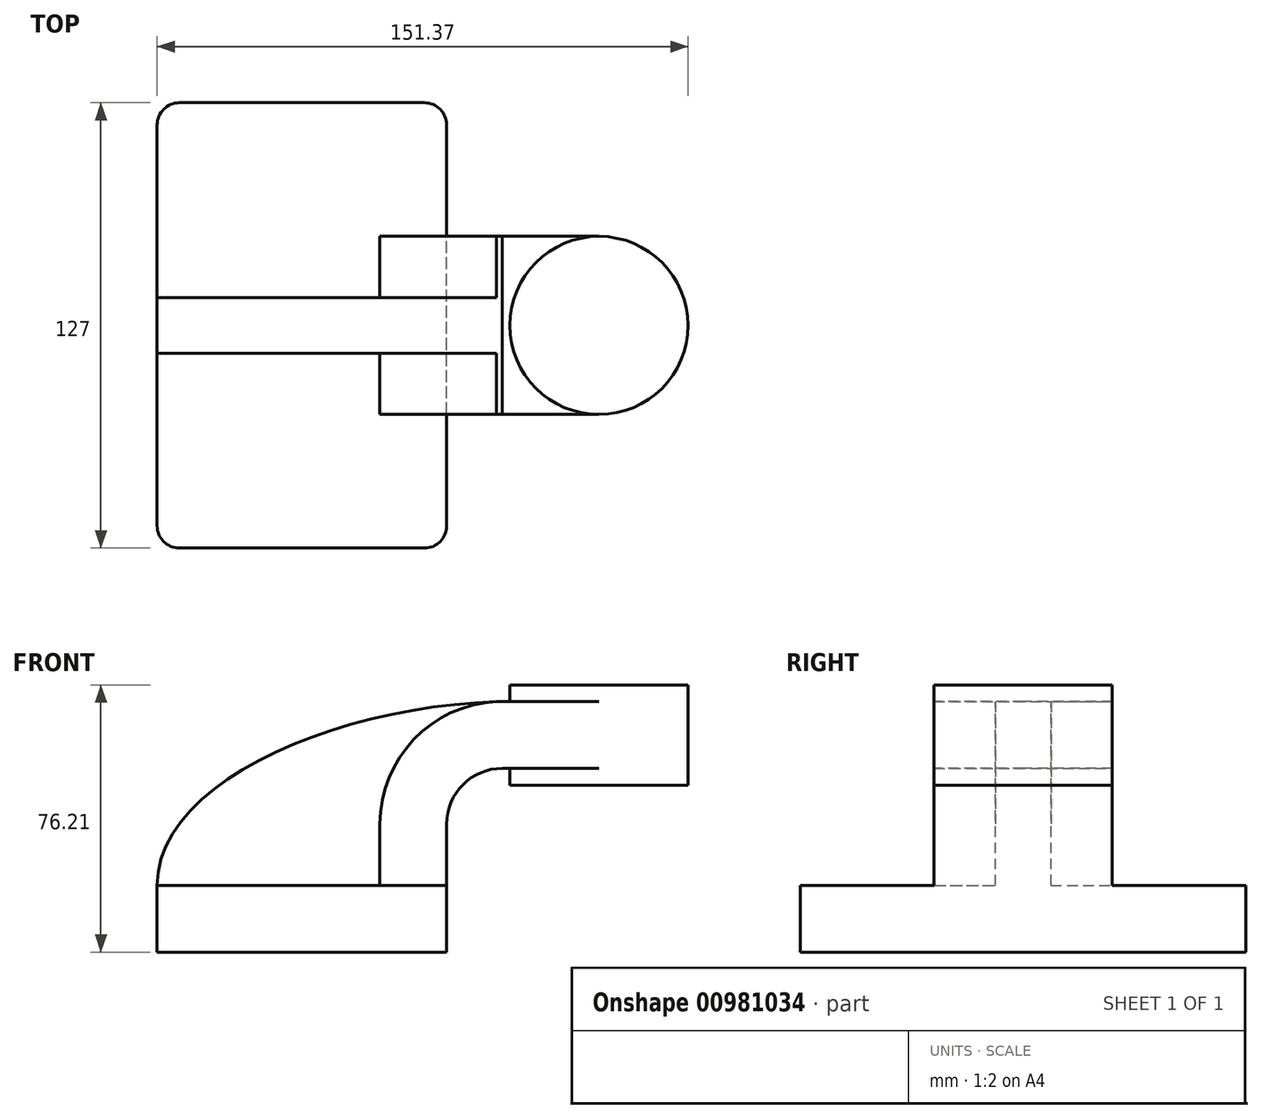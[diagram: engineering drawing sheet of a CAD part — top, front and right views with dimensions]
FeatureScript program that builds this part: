
annotation { "Feature Type Name" : "Feature", "Feature Type Description" : "" }
export const myFeature = defineFeature(function(context is Context, id is Id, definition is map)
    precondition{}
    {
        {
            var Q0;
            Q0=qCreatedBy(makeId("Front.planeOp"),FACE);
            var sketch = newSketch(context, id + "F0", { "sketchPlane" : qUnion([Q0])});
            skLineSegment(sketch, "E0.bottom", {"start": v(-41.28, 9.52) * mm, "end": v(41.28, 9.53) * mm});
            skLineSegment(sketch, "E0.top", {"start": v(-41.27, -9.52) * mm, "end": v(41.28, -9.52) * mm});
            skLineSegment(sketch, "E0.left", {"start": v(-41.28, 9.52) * mm, "end": v(-41.28, -9.52) * mm});
            skLineSegment(sketch, "E0.right", {"start": v(41.27, 9.53) * mm, "end": v(41.28, -9.52) * mm});
            skPoint(sketch, "E0.middle", {"position": v(0, 0) * mm});
            skLineSegment(sketch, "E1.bottom", {"start": v(110.09, 38.1) * mm, "end": v(59.29, 38.1) * mm});
            skLineSegment(sketch, "E1.top", {"start": v(110.09, 66.68) * mm, "end": v(59.29, 66.68) * mm});
            skLineSegment(sketch, "E1.left", {"start": v(110.09, 38.1) * mm, "end": v(110.09, 66.68) * mm});
            skLineSegment(sketch, "E1.right", {"start": v(59.29, 38.1) * mm, "end": v(59.29, 66.68) * mm});
            skPoint(sketch, "E1.middle", {"position": v(84.69, 52.39) * mm});
            skLineSegment(sketch, "E2", {"start": v(41.27, 9.53) * mm, "end": v(41.27, 27) * mm});
            skArc(sketch, "E3", {"start": v(41.27, 27) * mm, "mid": v(45.92, 38.23) * mm, "end": v(57.15, 42.88) * mm});
            skLineSegment(sketch, "E4", {"start": v(57.15, 42.88) * mm, "end": v(84.69, 42.88) * mm});
            skPoint(sketch, "E4.endSnap0", {"position": v(84.69, 38.1) * mm});
            skLineSegment(sketch, "E5.0", {"start": v(57.15, 61.93) * mm, "end": v(84.69, 61.93) * mm});
            skArc(sketch, "E5.1", {"start": v(22.22, 27) * mm, "mid": v(32.45, 51.7) * mm, "end": v(57.15, 61.93) * mm});
            skLineSegment(sketch, "E5.2", {"start": v(22.22, 9.53) * mm, "end": v(22.22, 27) * mm});
            skLineSegment(sketch, "E6", {"start": v(84.69, 38.1) * mm, "end": v(84.69, 66.68) * mm});
            skFitSpline(sketch, "E7", {"points": [v(-41.28, 9.53) * mm, v(57.15, 61.93) * mm], "startDerivative": vector(0.15, 89.7) * mm, "endDerivative": vector(137.76, 2.53) * mm});
            skSolve(sketch);
        }
        {
            var Q0;
            Q0=makeQuery(id+"F0.imprint","IMPRINT",FACE,{"disambiguationData":[TD([[makeQuery(id+"F0.imprint","IMPRINT",EDGE,{"derivedFrom":sQuery(id+"F0.wireOp",EDGE,"E0.top")}),1.0]])]});
            extrude(context, id + "F1", {"entities" : qUnion([Q0]), "endBound" : BoundingType.SYMMETRIC, "depth" : 127 * mm, "offsetDistance" : 25.4 * mm});
        }
        {
            var Q0;
            {var subQ3=sQuery(id+"F0.wireOp",EDGE,"E5.2");Q0=makeQuery(id+"F0.imprint","IMPRINT",FACE,{"disambiguationData":[TD([[makeQuery(id+"F0.imprint","IMPRINT",EDGE,{"derivedFrom":subQ3}),1.0]])]});}
            extrude(context, id + "F2", {"entities" : qUnion([Q0]), "operationType" : NewBodyOperationType.ADD, "endBound" : BoundingType.SYMMETRIC, "depth" : 15.88 * mm, "offsetDistance" : 25.4 * mm});
        }
        {
            var Q0;
            Q0=makeQuery(id+"F1.opExtrude","CAP_EDGE",EDGE,{"disambiguationData":[OSD([sQuery(id+"F0.wireOp",EDGE,"E0.left")])],"isStart":false});
            var Q1;
            Q1=makeQuery(id+"F1.opExtrude","CAP_EDGE",EDGE,{"disambiguationData":[OSD([sQuery(id+"F0.wireOp",EDGE,"E0.right")])],"isStart":false});
            var Q2;
            Q2=makeQuery(id+"F1.opExtrude","CAP_EDGE",EDGE,{"disambiguationData":[OSD([sQuery(id+"F0.wireOp",EDGE,"E0.right")])],"isStart":true});
            var Q3;
            Q3=makeQuery(id+"F1.opExtrude","CAP_EDGE",EDGE,{"disambiguationData":[OSD([sQuery(id+"F0.wireOp",EDGE,"E0.left")])],"isStart":true});
            fillet(context, id + "F3", {"entities" : qUnion([Q0, Q1, Q2, Q3]), "radius" : 6.35 * mm, "tangentPropagation" : true, "allowEdgeOverflow" : false});
        }
        {
            var Q0;
            {var subQ1=sQuery(id+"F0.wireOp",EDGE,"E2");Q0=makeQuery(id+"F0.imprint","IMPRINT",FACE,{"disambiguationData":[TD([[makeQuery(id+"F0.imprint","IMPRINT",EDGE,{"derivedFrom":subQ1}),1.0]])]});}
            var Q1;
            {var subQ0=sQuery(id+"F0.wireOp",EDGE,"E4");var subQ1=sQuery(id+"F0.wireOp",EDGE,"E1.right");var subQ2=makeQuery(id+"F0.imprint","INTERSECT",VERTEX,{"derivedFrom":[subQ1,subQ0]});Q1=makeQuery(id+"F0.imprint","IMPRINT",FACE,{"disambiguationData":[TD([[makeQuery(id+"F0.imprint","IMPRINT",EDGE,{"disambiguationData":[TD([[subQ2,-1.0]])],"derivedFrom":subQ1}),-1.0]])]});}
            extrude(context, id + "F4", {"entities" : qUnion([Q0, Q1]), "operationType" : NewBodyOperationType.ADD, "endBound" : BoundingType.SYMMETRIC, "depth" : 50.8 * mm, "offsetDistance" : 25.4 * mm});
        }
        {
            var Q0;
            {var subQ0=sQuery(id+"F0.wireOp",EDGE,"E1.left");Q0=makeQuery(id+"F0.imprint","IMPRINT",FACE,{"disambiguationData":[TD([[makeQuery(id+"F0.imprint","IMPRINT",EDGE,{"derivedFrom":subQ0}),1.0]])]});}
            var Q1;
            Q1=sQuery(id+"F0.wireOp",EDGE,"E6");
            revolve(context, id + "F5", {"operationType" : NewBodyOperationType.ADD, "surfaceOperationType" : NewSurfaceOperationType.NEW, "entities" : qUnion([Q0]), "axis" : qUnion([Q1]), "revolveType" : RevolveType.FULL});
        }
    });
